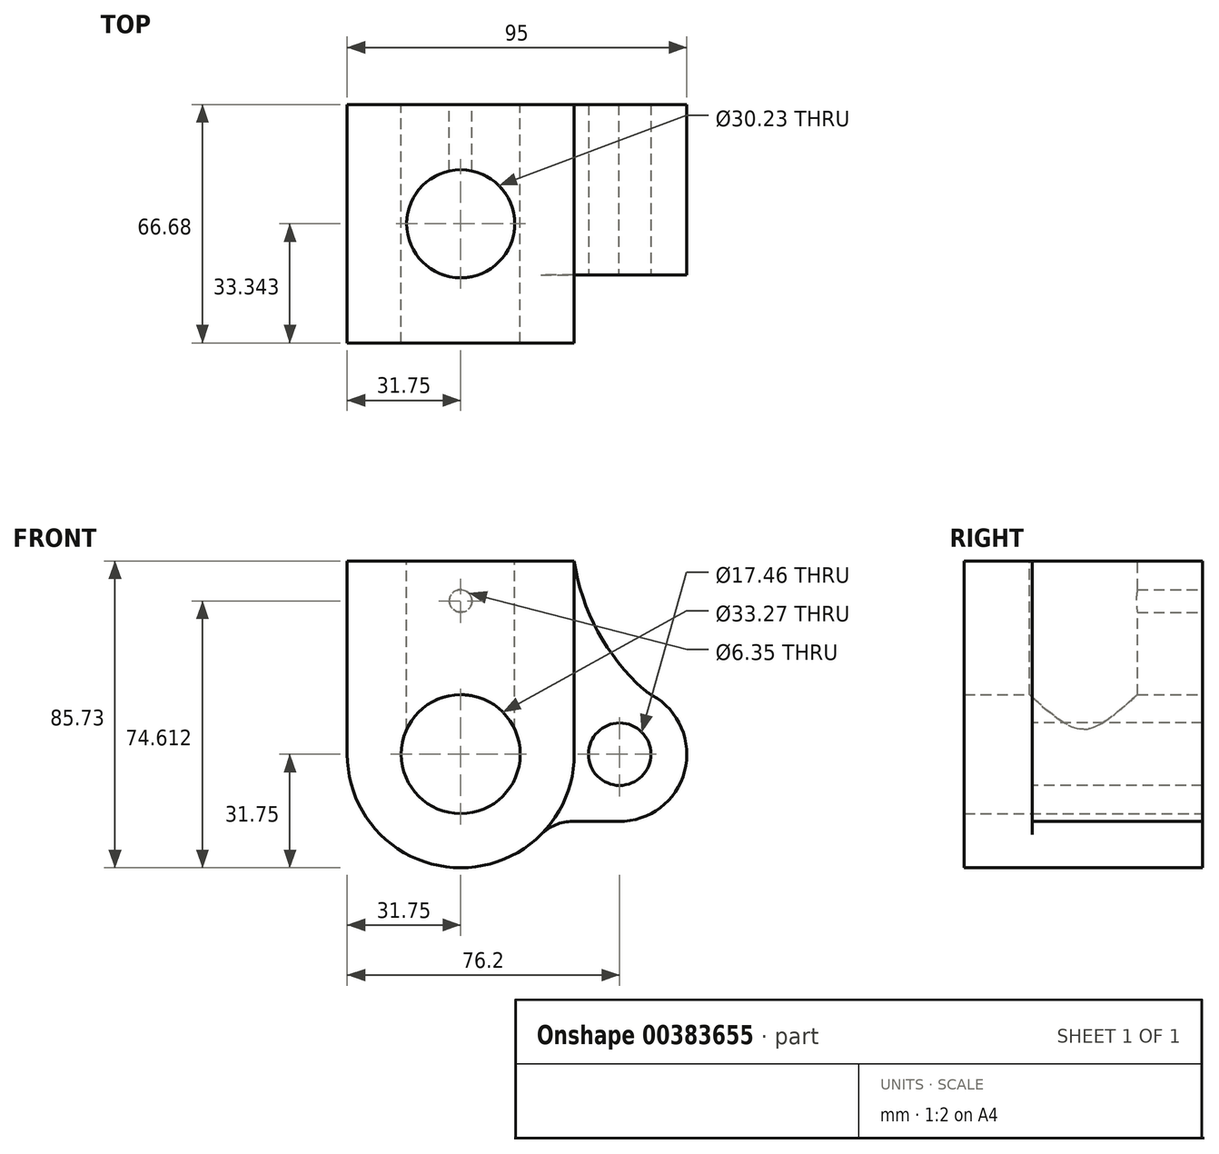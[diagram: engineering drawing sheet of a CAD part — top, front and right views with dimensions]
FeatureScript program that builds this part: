
annotation { "Feature Type Name" : "Feature", "Feature Type Description" : "" }
export const myFeature = defineFeature(function(context is Context, id is Id, definition is map)
    precondition{}
    {
        {
            var Q0;
            Q0=qCreatedBy(makeId("Front.planeOp"),FACE);
            var sketch = newSketch(context, id + "F0", { "sketchPlane" : qUnion([Q0])});
            skCircle(sketch, "E0", {"center": v(0, 0) * mm, "radius": 16.64 * mm});
            skCircle(sketch, "E1", {"center": v(0, 0) * mm, "radius": 63.5 * mm});
            skSolve(sketch);
        }
        {
            var Q0;
            Q0 = qSketchRegion(id + "F0", true);
            extrude(context, id + "F1", {"entities" : qUnion([Q0]), "depth" : 66.67 * mm});
        }
        {
            var Q0;
            Q0=makeQuery(id+"F1.opExtrude","CAP_FACE",FACE,{"disambiguationData":[OSD([sQuery(id+"F0.wireOp",EDGE,"E0"),sQuery(id+"F0.wireOp",EDGE,"E1")])],"isStart":false});
            var sketch = newSketch(context, id + "F2", { "sketchPlane" : qUnion([Q0])});
            skCircle(sketch, "E2", {"center": v(44.45, 0) * mm, "radius": 8.73 * mm});
            skLineSegment(sketch, "E3", {"start": v(-31.75, 53.98) * mm, "end": v(31.7, 53.98) * mm});
            skArc(sketch, "E4", {"start": v(44.21, -18.8) * mm, "mid": v(62.62, -4.8) * mm, "end": v(53.53, 16.46) * mm});
            skArc(sketch, "E5", {"start": v(-31.75, 0) * mm, "mid": v(-12.18, -29.32) * mm, "end": v(22.4, -22.5) * mm});
            skLineSegment(sketch, "E6", {"start": v(-31.75, 53.98) * mm, "end": v(-31.75, 0) * mm});
            skLineSegment(sketch, "E7", {"start": v(44.21, -18.8) * mm, "end": v(31.37, -18.8) * mm});
            skArc(sketch, "E8", {"start": v(31.7, 53.97) * mm, "mid": v(38.34, 34.34) * mm, "end": v(51.21, 18.1) * mm});
            skPoint(sketch, "E9.visualSharp", {"position": v(25.59, -18.8) * mm});
            skArc(sketch, "E9.filletArc", {"start": v(31.37, -18.8) * mm, "mid": v(26.52, -19.76) * mm, "end": v(22.4, -22.5) * mm});
            skPoint(sketch, "E10.visualSharp", {"position": v(52.5, 16.99) * mm});
            skArc(sketch, "E10.filletArc", {"start": v(51.21, 18.1) * mm, "mid": v(52.32, 17.21) * mm, "end": v(53.53, 16.46) * mm});
            skCircle(sketch, "E11", {"center": v(0, 0) * mm, "radius": 63.5 * mm});
            skSolve(sketch);
        }
        {
            var Q0;
            Q0=makeQuery(id+"F2.imprint","IMPRINT",FACE,{"disambiguationData":[TD([[makeQuery(id+"F2.imprint","IMPRINT",EDGE,{"derivedFrom":sQuery(id+"F2.wireOp",EDGE,"E3")}),1.0]])]});
            var Q1;
            Q1=makeQuery(id+"F2.imprint","IMPRINT",FACE,{"disambiguationData":[TD([[makeQuery(id+"F2.imprint","IMPRINT",EDGE,{"derivedFrom":sQuery(id+"F2.wireOp",EDGE,"E2")}),1.0]])]});
            extrude(context, id + "F3", {"entities" : qUnion([Q0, Q1]), "operationType" : NewBodyOperationType.REMOVE, "endBound" : BoundingType.THROUGH_ALL, "oppositeDirection" : true, "depth" : 25.4 * mm});
        }
        {
            var Q0;
            Q0=makeQuery(id+"F1.opExtrude","CAP_FACE",FACE,{"disambiguationData":[OSD([sQuery(id+"F0.wireOp",EDGE,"E0"),sQuery(id+"F0.wireOp",EDGE,"E1")])],"isStart":false});
            var sketch = newSketch(context, id + "F4", { "sketchPlane" : qUnion([Q0])});
            skArc(sketch, "E12.0", {"start": v(44.21, -18.8) * mm, "mid": v(62.62, -4.8) * mm, "end": v(53.53, 16.46) * mm});
            skLineSegment(sketch, "E13.0", {"start": v(44.21, -18.8) * mm, "end": v(31.37, -18.8) * mm});
            skPoint(sketch, "E14.0.end.orphan", {"position": v(22.4, -22.5) * mm});
            skPoint(sketch, "E14.0.start.orphan", {"position": v(-31.75, 0) * mm});
            skArc(sketch, "E15", {"start": v(22.4, -22.5) * mm, "mid": v(29.33, -12.15) * mm, "end": v(31.75, 0.06) * mm});
            skLineSegment(sketch, "E16", {"start": v(31.75, 0) * mm, "end": v(31.7, 53.97) * mm});
            skArc(sketch, "E17.0", {"start": v(31.7, 53.97) * mm, "mid": v(38.34, 34.34) * mm, "end": v(51.21, 18.1) * mm});
            skArc(sketch, "E18.0", {"start": v(51.21, 18.1) * mm, "mid": v(52.32, 17.21) * mm, "end": v(53.53, 16.46) * mm});
            skArc(sketch, "E19.0", {"start": v(31.37, -18.8) * mm, "mid": v(26.52, -19.76) * mm, "end": v(22.4, -22.5) * mm});
            skCircle(sketch, "E20.0", {"center": v(44.45, 0) * mm, "radius": 8.73 * mm});
            skSolve(sketch);
        }
        {
            var Q0;
            Q0 = qSketchRegion(id + "F4", true);
            extrude(context, id + "F5", {"entities" : qUnion([Q0]), "operationType" : NewBodyOperationType.REMOVE, "oppositeDirection" : true, "depth" : 19.05 * mm});
        }
        {
            var Q0;
            Q0=makeQuery(id+"F1.opExtrude","CAP_FACE",FACE,{"disambiguationData":[OSD([sQuery(id+"F0.wireOp",EDGE,"E0"),sQuery(id+"F0.wireOp",EDGE,"E1")])],"isStart":false});
            cPlane(context, id + "F6", {"entities" : qUnion([Q0]), "cplaneType" : CPlaneType.OFFSET, "offset" : 33.34 * mm, "oppositeDirection" : true, "width" : 152.4 * mm, "height" : 152.4 * mm});
        }
        {
            var Q0;
            Q0=makeQuery(id+"F3.boolean.opBoolean","COPY",FACE,{"derivedFrom":makeQuery(id+"F3.opExtrude","SWEPT_FACE",FACE,{"disambiguationData":[OSD([sQuery(id+"F2.wireOp",EDGE,"E3")])]})});
            var sketch = newSketch(context, id + "F7", { "sketchPlane" : qUnion([Q0])});
            skCircle(sketch, "E21", {"center": v(0, -33.34) * mm, "radius": 15.12 * mm});
            skLineSegment(sketch, "E22", {"start": v(16.64, 0) * mm, "end": v(16.64, -66.68) * mm});
            skLineSegment(sketch, "E23", {"start": v(-16.64, -66.68) * mm, "end": v(-16.64, 0) * mm});
            skSolve(sketch);
        }
        {
            var Q0;
            Q0 = qSketchRegion(id + "F7", true);
            extrude(context, id + "F8", {"entities" : qUnion([Q0]), "operationType" : NewBodyOperationType.REMOVE, "oppositeDirection" : true, "depth" : 53.6 * mm});
        }
        {
            var Q0;
            Q0=makeQuery(id+"F1.opExtrude","CAP_FACE",FACE,{"disambiguationData":[OSD([sQuery(id+"F0.wireOp",EDGE,"E0"),sQuery(id+"F0.wireOp",EDGE,"E1")])],"isStart":true});
            var sketch = newSketch(context, id + "F9", { "sketchPlane" : qUnion([Q0])});
            skCircle(sketch, "E24", {"center": v(0, 42.86) * mm, "radius": 3.18 * mm});
            skSolve(sketch);
        }
        {
            var Q0;
            Q0 = qSketchRegion(id + "F9", true);
            extrude(context, id + "F10", {"entities" : qUnion([Q0]), "operationType" : NewBodyOperationType.REMOVE, "oppositeDirection" : true, "depth" : 25.4 * mm});
        }
    });
